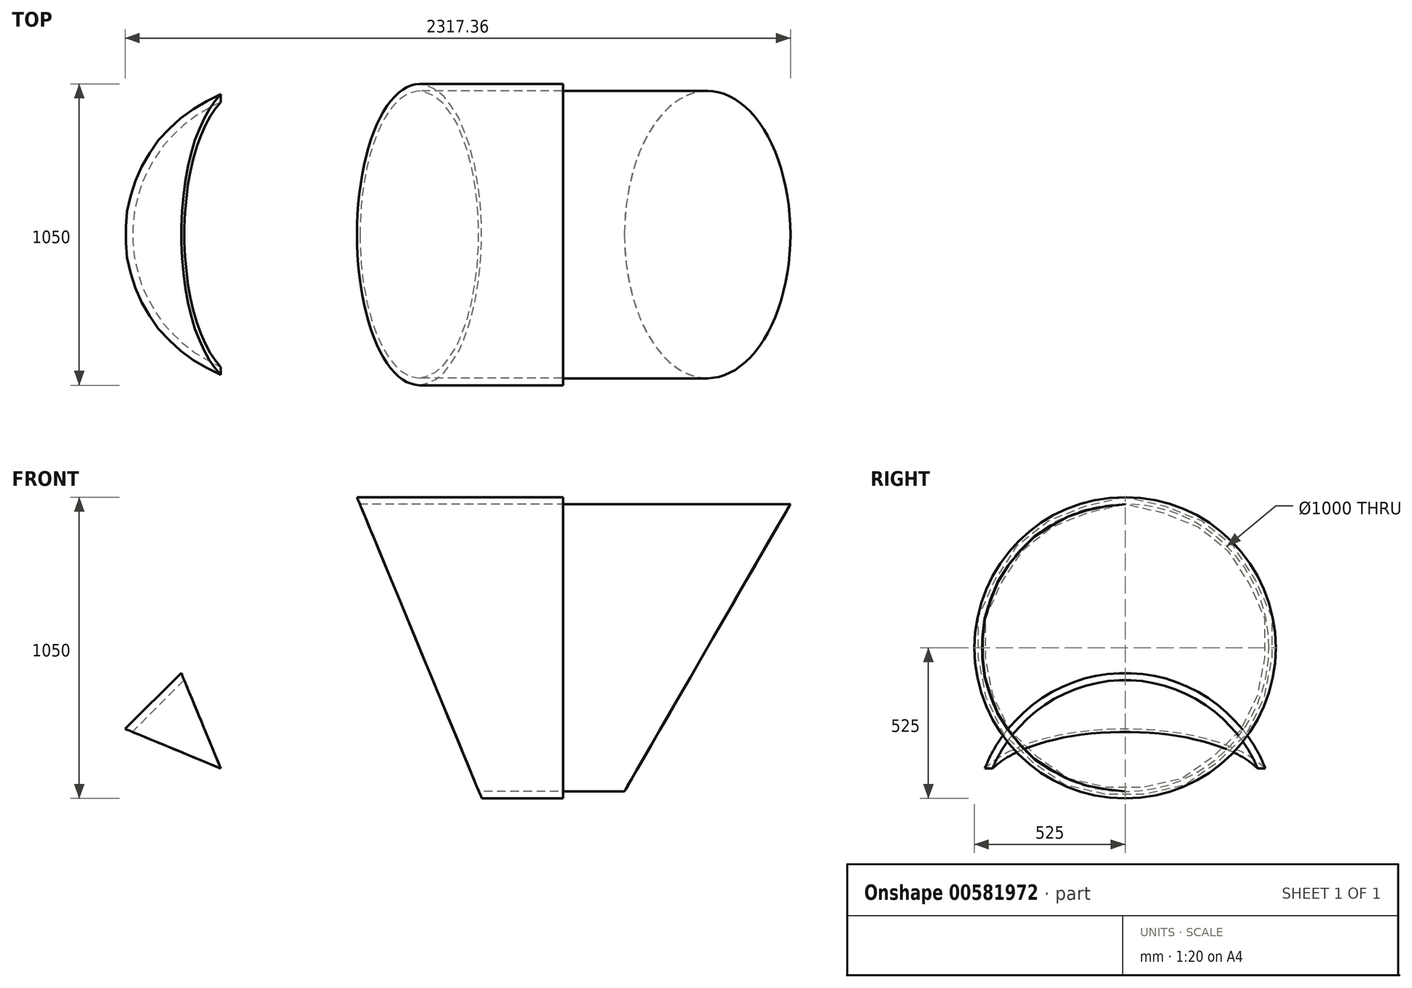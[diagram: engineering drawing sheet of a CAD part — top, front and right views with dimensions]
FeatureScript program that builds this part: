
annotation { "Feature Type Name" : "Feature", "Feature Type Description" : "" }
export const myFeature = defineFeature(function(context is Context, id is Id, definition is map)
    precondition{}
    {
        {
            var Q0;
            Q0=qCreatedBy(makeId("Front.planeOp"),FACE);
            var sketch = newSketch(context, id + "F0", { "sketchPlane" : qUnion([Q0])});
            skLineSegment(sketch, "E0", {"start": v(0, 0) * mm, "end": v(0, -525.84) * mm, "construction": true});
            skLineSegment(sketch, "E1", {"start": v(-525, -1040) * mm, "end": v(-524, -1040) * mm});
            skLineSegment(sketch, "E2", {"start": v(-524, -1040) * mm, "end": v(-524, -1000) * mm});
            skLineSegment(sketch, "E3", {"start": v(-524, -1000) * mm, "end": v(-501, -1000) * mm});
            skLineSegment(sketch, "E4", {"start": v(-501, -1000) * mm, "end": v(-501, -1040) * mm});
            skLineSegment(sketch, "E5", {"start": v(-501, -1040) * mm, "end": v(-500, -1040) * mm});
            skLineSegment(sketch, "E6", {"start": v(0, 0) * mm, "end": v(-755.87, 0) * mm, "construction": true});
            skLineSegment(sketch, "E7", {"start": v(-525, -1040) * mm, "end": v(-525, -282.54) * mm});
            skLineSegment(sketch, "E8", {"start": v(-500, -1040) * mm, "end": v(-500, -292.9) * mm});
            skLineSegment(sketch, "E9", {"start": v(0, 0) * mm, "end": v(738.22, 0) * mm, "construction": true});
            skLineSegment(sketch, "E10", {"start": v(509, 501) * mm, "end": v(1000, 501) * mm});
            skLineSegment(sketch, "E11", {"start": v(1000, 501) * mm, "end": v(1000, 524) * mm});
            skLineSegment(sketch, "E12", {"start": v(1000, 524) * mm, "end": v(1000, 524) * mm});
            skLineSegment(sketch, "E13", {"start": v(1000, 524) * mm, "end": v(1000, 525) * mm});
            skLineSegment(sketch, "E14", {"start": v(1000, 525) * mm, "end": v(282.54, 525) * mm});
            skLineSegment(sketch, "E15", {"start": v(-500, -292.9) * mm, "end": v(292.9, 500) * mm});
            skLineSegment(sketch, "E16", {"start": v(-500, -292.9) * mm, "end": v(-916.78, -120.26) * mm, "construction": true});
            skLineSegment(sketch, "E17", {"start": v(-500, -292.9) * mm, "end": v(-908.83, -292.9) * mm, "construction": true});
            skLineSegment(sketch, "E18", {"start": v(-500, -292.9) * mm, "end": v(-525, -282.54) * mm});
            skLineSegment(sketch, "E19", {"start": v(292.9, 500) * mm, "end": v(292.9, 943.16) * mm, "construction": true});
            skLineSegment(sketch, "E20", {"start": v(292.9, 500) * mm, "end": v(126.22, 902.38) * mm, "construction": true});
            skLineSegment(sketch, "E21", {"start": v(292.9, 500) * mm, "end": v(282.54, 525) * mm});
            skLineSegment(sketch, "E22.trimOffspring", {"start": v(292.9, 500) * mm, "end": v(1000, 500) * mm});
            skLineSegment(sketch, "E23", {"start": v(-525, -282.54) * mm, "end": v(282.54, 525) * mm});
            skLineSegment(sketch, "E24", {"start": v(-500, -292.9) * mm, "end": v(711.1, -794.54) * mm, "construction": true});
            skLineSegment(sketch, "E25", {"start": v(292.9, 500) * mm, "end": v(744.2, -589.53) * mm, "construction": true});
            skLineSegment(sketch, "E26", {"start": v(0, -500) * mm, "end": v(500, 0) * mm, "construction": true});
            skLineSegment(sketch, "E27", {"start": v(509, 501) * mm, "end": v(2000, 501) * mm});
            skLineSegment(sketch, "E28", {"start": v(1000, 500) * mm, "end": v(2000, 500) * mm});
            skLineSegment(sketch, "E29", {"start": v(2000, 500) * mm, "end": v(2000, 501) * mm});
            skSolve(sketch);
        }
        {
            var Q0;
            Q0=qCreatedBy(makeId("Right.planeOp"),FACE);
            var sketch = newSketch(context, id + "F1", { "sketchPlane" : qUnion([Q0])});
            skLineSegment(sketch, "E30", {"start": v(288.35, -500) * mm, "end": v(-360.5, -500) * mm, "construction": true});
            skSolve(sketch);
        }
        {
            var Q0;
            Q0=sQuery(id+"F1.wireOp",EDGE,"E30");
            var Q1;
            Q1=sQuery(id+"F0.wireOp",EDGE,"E24");
            cPlane(context, id + "F2", {"entities" : qUnion([Q0, Q1]), "cplaneType" : CPlaneType.LINE_ANGLE, "offset" : 25 * mm, "angle" : 0 * degree, "width" : 150 * mm, "height" : 150 * mm});
        }
        {
            var Q0;
            Q0=qCreatedBy(makeId("Top.planeOp"),FACE);
            var sketch = newSketch(context, id + "F3", { "sketchPlane" : qUnion([Q0])});
            skLineSegment(sketch, "E31", {"start": v(500, 508.47) * mm, "end": v(500, -612.1) * mm, "construction": true});
            skSolve(sketch);
        }
        {
            var Q0;
            Q0=sQuery(id+"F3.wireOp",EDGE,"E31");
            var Q1;
            Q1=sQuery(id+"F0.wireOp",EDGE,"E25");
            cPlane(context, id + "F4", {"entities" : qUnion([Q0, Q1]), "cplaneType" : CPlaneType.LINE_ANGLE, "offset" : 25 * mm, "angle" : 0 * degree, "width" : 150 * mm, "height" : 150 * mm});
        }
        {
            var Q0;
            Q0=qCreatedBy(id+"F2.planeOp",FACE);
            var sketch = newSketch(context, id + "F5", { "sketchPlane" : qUnion([Q0])});
            skLineSegment(sketch, "E32.bottom", {"start": v(-815.8, -791.8) * mm, "end": v(1036.86, -791.8) * mm});
            skLineSegment(sketch, "E32.top", {"start": v(-815.8, 744.83) * mm, "end": v(1036.86, 744.83) * mm});
            skLineSegment(sketch, "E32.left", {"start": v(-815.8, -791.8) * mm, "end": v(-815.8, 744.83) * mm});
            skLineSegment(sketch, "E32.right", {"start": v(1036.86, -791.8) * mm, "end": v(1036.86, 744.83) * mm});
            skSolve(sketch);
        }
        {
            var Q0;
            Q0=qCreatedBy(id+"F4.planeOp",FACE);
            var sketch = newSketch(context, id + "F6", { "sketchPlane" : qUnion([Q0])});
            skLineSegment(sketch, "E33.bottom", {"start": v(754.29, -977.32) * mm, "end": v(-876.24, -977.32) * mm});
            skLineSegment(sketch, "E33.top", {"start": v(754.29, 712.75) * mm, "end": v(-876.24, 712.75) * mm});
            skLineSegment(sketch, "E33.left", {"start": v(754.29, -977.32) * mm, "end": v(754.29, 712.75) * mm});
            skLineSegment(sketch, "E33.right", {"start": v(-876.24, -977.32) * mm, "end": v(-876.24, 712.75) * mm});
            skSolve(sketch);
        }
        {
            var Q0;
            Q0=makeQuery(id+"F0.imprint","IMPRINT",FACE,{"disambiguationData":[TD([[makeQuery(id+"F0.imprint","IMPRINT",EDGE,{"derivedFrom":sQuery(id+"F0.wireOp",EDGE,"E1")}),1.0]])]});
            var Q1;
            Q1=sQuery(id+"F0.wireOp",EDGE,"E0");
            revolve(context, id + "F7", {"surfaceOperationType" : NewSurfaceOperationType.NEW, "entities" : qUnion([Q0]), "axis" : qUnion([Q1]), "revolveType" : RevolveType.FULL});
        }
        {
            var Q0;
            Q0=makeQuery(id+"F5.imprint","IMPRINT",FACE,{"disambiguationData":[TD([[makeQuery(id+"F5.imprint","IMPRINT",EDGE,{"derivedFrom":sQuery(id+"F5.wireOp",EDGE,"E32.bottom")}),1.0]])]});
            var Q1;
            Q1=makeQuery(id+"F7.opRevolve","SWEPT_BODY",BODY,{"disambiguationData":[OSD([sQuery(id+"F0.wireOp",EDGE,"E1"),sQuery(id+"F0.wireOp",EDGE,"E2"),sQuery(id+"F0.wireOp",EDGE,"E3"),sQuery(id+"F0.wireOp",EDGE,"E4"),sQuery(id+"F0.wireOp",EDGE,"E5"),sQuery(id+"F0.wireOp",EDGE,"E7"),sQuery(id+"F0.wireOp",EDGE,"E8"),sQuery(id+"F0.wireOp",EDGE,"E18")])]});
            extrude(context, id + "F8", {"entities" : qUnion([Q0]), "operationType" : NewBodyOperationType.REMOVE, "endBoundEntityBody" : qUnion([Q1]), "offsetDistance" : 25 * mm, "depth" : 1120 * mm});
        }
        {
            var Q0;
            Q0=makeQuery(id+"F0.imprint","IMPRINT",FACE,{"disambiguationData":[TD([[makeQuery(id+"F0.imprint","IMPRINT",EDGE,{"derivedFrom":sQuery(id+"F0.wireOp",EDGE,"E15")}),1.0]])]});
            var Q1;
            Q1=sQuery(id+"F0.wireOp",EDGE,"E26");
            revolve(context, id + "F9", {"surfaceOperationType" : NewSurfaceOperationType.NEW, "entities" : qUnion([Q0]), "axis" : qUnion([Q1]), "revolveType" : RevolveType.FULL});
        }
        {
            var Q0;
            Q0=makeQuery(id+"F5.imprint","IMPRINT",FACE,{"disambiguationData":[TD([[makeQuery(id+"F5.imprint","IMPRINT",EDGE,{"derivedFrom":sQuery(id+"F5.wireOp",EDGE,"E32.bottom")}),1.0]])]});
            extrude(context, id + "F10", {"entities" : qUnion([Q0]), "operationType" : NewBodyOperationType.REMOVE, "oppositeDirection" : true, "offsetDistance" : 25 * mm, "depth" : 730 * mm});
        }
        {
            var Q0;
            Q0=makeQuery(id+"F6.imprint","IMPRINT",FACE,{"disambiguationData":[TD([[makeQuery(id+"F6.imprint","IMPRINT",EDGE,{"derivedFrom":sQuery(id+"F6.wireOp",EDGE,"E33.bottom")}),-1.0]])]});
            extrude(context, id + "F11", {"entities" : qUnion([Q0]), "operationType" : NewBodyOperationType.REMOVE, "offsetDistance" : 25 * mm, "depth" : 750 * mm});
        }
        {
            var Q0;
            Q0=makeQuery(id+"F0.imprint","IMPRINT",FACE,{"disambiguationData":[TD([[makeQuery(id+"F0.imprint","IMPRINT",EDGE,{"derivedFrom":sQuery(id+"F0.wireOp",EDGE,"E11")}),1.0]])]});
            var Q1;
            Q1=sQuery(id+"F0.wireOp",EDGE,"E9");
            revolve(context, id + "F12", {"surfaceOperationType" : NewSurfaceOperationType.NEW, "entities" : qUnion([Q0]), "axis" : qUnion([Q1]), "revolveType" : RevolveType.FULL});
        }
        {
            var Q0;
            Q0=makeQuery(id+"F6.imprint","IMPRINT",FACE,{"disambiguationData":[TD([[makeQuery(id+"F6.imprint","IMPRINT",EDGE,{"derivedFrom":sQuery(id+"F6.wireOp",EDGE,"E33.bottom")}),-1.0]])]});
            extrude(context, id + "F13", {"entities" : qUnion([Q0]), "operationType" : NewBodyOperationType.REMOVE, "oppositeDirection" : true, "offsetDistance" : 25 * mm, "depth" : 800 * mm});
        }
        {
            var Q0;
            Q0=qCreatedBy(makeId("Front.planeOp"),FACE);
            var sketch = newSketch(context, id + "F14", { "sketchPlane" : qUnion([Q0])});
            skLineSegment(sketch, "E34.0", {"start": v(1000, -525) * mm, "end": v(1000, 525) * mm, "construction": true});
            skLineSegment(sketch, "E35", {"start": v(1200, -525) * mm, "end": v(1806.22, 525) * mm});
            skLineSegment(sketch, "E36", {"start": v(1806.22, 525) * mm, "end": v(2100, 525) * mm});
            skLineSegment(sketch, "E37", {"start": v(2100, 525) * mm, "end": v(2100, -525) * mm});
            skLineSegment(sketch, "E38", {"start": v(2100, -525) * mm, "end": v(1200, -525) * mm});
            skSolve(sketch);
        }
        {
            var Q0;
            Q0 = qSketchRegion(id + "F14", true);
            extrude(context, id + "F15", {"entities" : qUnion([Q0]), "operationType" : NewBodyOperationType.REMOVE, "depth" : 1200 * mm, "offsetDistance" : 25 * mm, "symmetric" : true});
        }
    });
